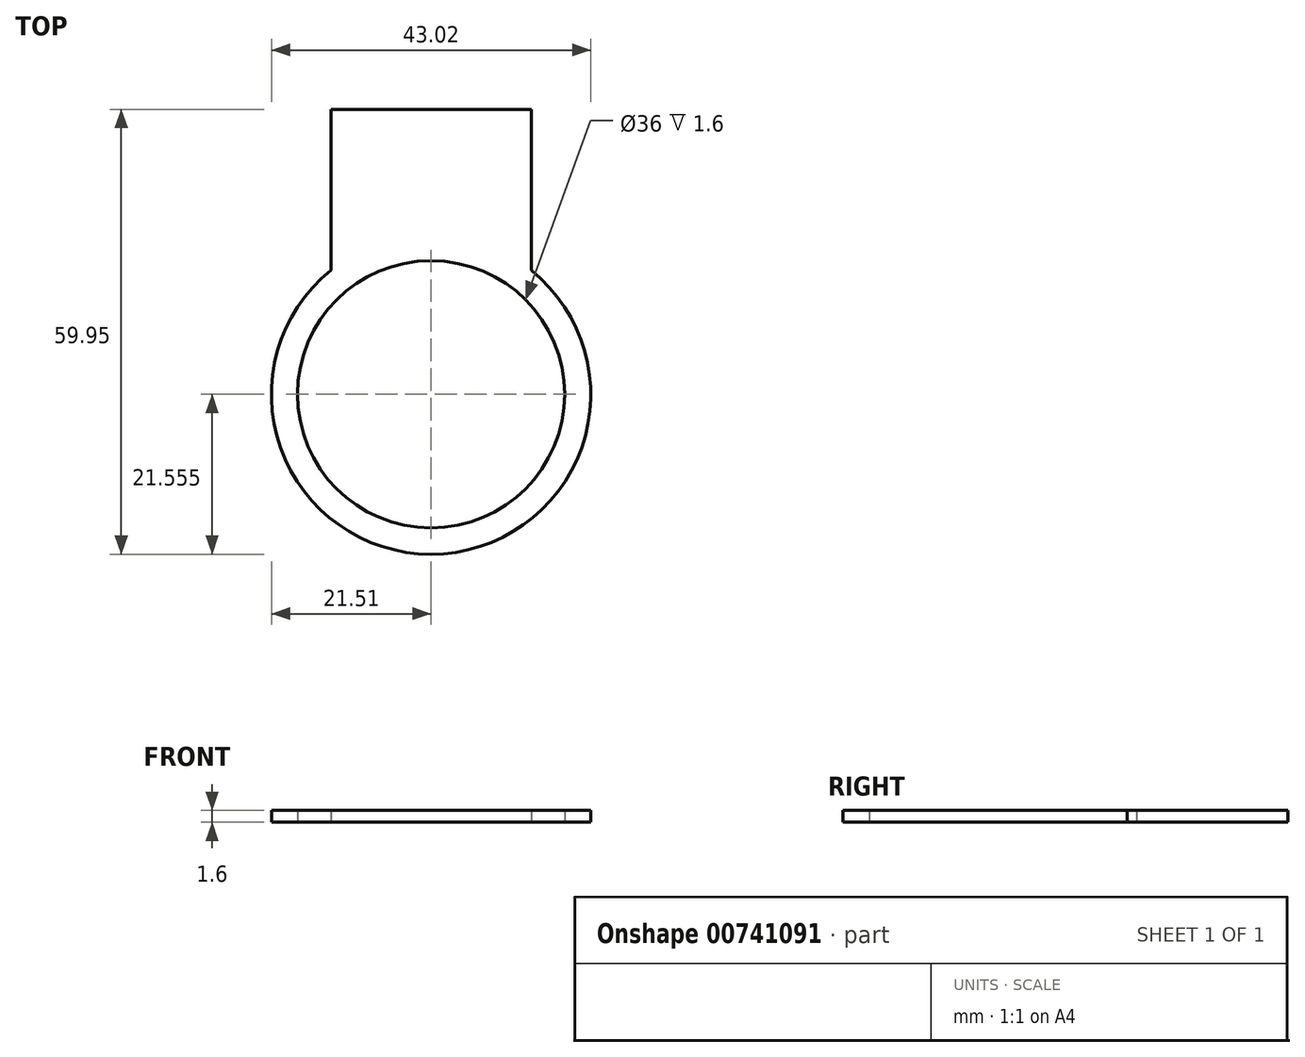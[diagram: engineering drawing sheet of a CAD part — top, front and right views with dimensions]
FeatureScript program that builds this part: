
annotation { "Feature Type Name" : "Feature", "Feature Type Description" : "" }
export const myFeature = defineFeature(function(context is Context, id is Id, definition is map)
    precondition{}
    {
        {
            var Q0;
            Q0=qCreatedBy(makeId("Top.planeOp"),FACE);
            var sketch = newSketch(context, id + "F0", { "sketchPlane" : qUnion([Q0])});
            skArc(sketch, "E0", {"start": v(-13.5, 8.26) * mm, "mid": v(0, -29.99) * mm, "end": v(13.5, 8.26) * mm});
            skLineSegment(sketch, "E1", {"start": v(13.5, 8.26) * mm, "end": v(13.5, 29.96) * mm});
            skArc(sketch, "E2", {"start": v(13.53, 29.96) * mm, "mid": v(13.5, 29.99) * mm, "end": v(13.47, 29.96) * mm});
            skLineSegment(sketch, "E3", {"start": v(-13.5, 29.96) * mm, "end": v(13.5, 29.96) * mm});
            skArc(sketch, "E4", {"start": v(13.5, 29.94) * mm, "mid": v(13.53, 29.96) * mm, "end": v(13.5, 29.99) * mm});
            skArc(sketch, "E5", {"start": v(-13.5, 29.99) * mm, "mid": v(-13.53, 29.96) * mm, "end": v(-13.5, 29.94) * mm});
            skLineSegment(sketch, "E6", {"start": v(-13.5, 8.26) * mm, "end": v(-13.5, 29.96) * mm});
            skArc(sketch, "E7", {"start": v(-13.48, 29.96) * mm, "mid": v(-13.5, 29.99) * mm, "end": v(-13.53, 29.96) * mm});
            skLineSegment(sketch, "E8", {"start": v(6.4, 18.46) * mm, "end": v(6.4, 19.26) * mm});
            skArc(sketch, "E9", {"start": v(6.42, 19.26) * mm, "mid": v(6.4, 19.29) * mm, "end": v(6.37, 19.26) * mm});
            skArc(sketch, "E10", {"start": v(6.37, 18.46) * mm, "mid": v(6.4, 18.44) * mm, "end": v(6.42, 18.46) * mm});
            skLineSegment(sketch, "E11", {"start": v(6.8, 18.86) * mm, "end": v(6, 18.86) * mm});
            skArc(sketch, "E12", {"start": v(6, 18.89) * mm, "mid": v(5.98, 18.86) * mm, "end": v(6, 18.84) * mm});
            skArc(sketch, "E13", {"start": v(6.8, 18.84) * mm, "mid": v(6.82, 18.86) * mm, "end": v(6.8, 18.89) * mm});
            skLineSegment(sketch, "E14", {"start": v(-6.8, 17.56) * mm, "end": v(-6.8, 18.96) * mm});
            skArc(sketch, "E15", {"start": v(-6.78, 18.96) * mm, "mid": v(-6.8, 18.99) * mm, "end": v(-6.83, 18.96) * mm});
            skArc(sketch, "E16", {"start": v(-6.83, 17.56) * mm, "mid": v(-6.8, 17.54) * mm, "end": v(-6.78, 17.56) * mm});
            skLineSegment(sketch, "E17", {"start": v(-7.5, 18.26) * mm, "end": v(-6.1, 18.26) * mm});
            skArc(sketch, "E18", {"start": v(-6.1, 18.24) * mm, "mid": v(-6.08, 18.26) * mm, "end": v(-6.1, 18.29) * mm});
            skArc(sketch, "E19", {"start": v(-7.5, 18.29) * mm, "mid": v(-7.53, 18.26) * mm, "end": v(-7.5, 18.24) * mm});
            skLineSegment(sketch, "E20", {"start": v(0, 18.16) * mm, "end": v(0, 20.36) * mm});
            skArc(sketch, "E21", {"start": v(0.03, 20.36) * mm, "mid": v(0, 20.39) * mm, "end": v(-0.03, 20.36) * mm});
            skArc(sketch, "E22", {"start": v(-0.03, 18.16) * mm, "mid": v(0, 18.14) * mm, "end": v(0.03, 18.16) * mm});
            skLineSegment(sketch, "E23", {"start": v(-1.1, 19.26) * mm, "end": v(1.1, 19.26) * mm});
            skArc(sketch, "E24", {"start": v(1.1, 19.24) * mm, "mid": v(1.12, 19.26) * mm, "end": v(1.1, 19.29) * mm});
            skArc(sketch, "E25", {"start": v(-1.1, 19.29) * mm, "mid": v(-1.13, 19.26) * mm, "end": v(-1.1, 19.24) * mm});
            skArc(sketch, "E26", {"start": v(0, -26.44) * mm, "mid": v(18, -8.44) * mm, "end": v(0, 9.56) * mm});
            skArc(sketch, "E27", {"start": v(0, 9.56) * mm, "mid": v(-18, -8.44) * mm, "end": v(0, -26.44) * mm});
            skSolve(sketch);
        }
        {
            var Q0;
            Q0=makeQuery(id+"F0.imprint","IMPRINT",FACE,{"disambiguationData":[TD([[makeQuery(id+"F0.imprint","IMPRINT",EDGE,{"derivedFrom":sQuery(id+"F0.wireOp",EDGE,"E26")}),-1.0]])]});
            extrude(context, id + "F1", {"entities" : qUnion([Q0]), "endBound" : BoundingType.SYMMETRIC, "depth" : 1.6 * mm, "offsetDistance" : 25 * mm});
        }
        {
            var Q0;
            Q0=makeQuery(id+"F1.opExtrude","CAP_FACE",FACE,{"disambiguationData":[OSD([sQuery(id+"F0.wireOp",EDGE,"E1"),sQuery(id+"F0.wireOp",EDGE,"ceca2dc5-4b51-4d0a-9e0b-030013c7a3e1"),sQuery(id+"F0.wireOp",EDGE,"E0"),sQuery(id+"F0.wireOp",EDGE,"8e6bffbf-1e1e-4fdc-b5db-a0290b015a5f"),sQuery(id+"F0.wireOp",EDGE,"db5c325e-766a-4718-8a78-7daab6099a77"),sQuery(id+"F0.wireOp",EDGE,"E3"),sQuery(id+"F0.wireOp",EDGE,"E6"),sQuery(id+"F0.wireOp",EDGE,"444f205d-ef0d-461a-a2ca-11d23d385707"),sQuery(id+"F0.wireOp",EDGE,"E26"),sQuery(id+"F0.wireOp",EDGE,"E27")])],"isStart":true});
            var sketch = newSketch(context, id + "F2", { "sketchPlane" : qUnion([Q0])});
            skLineSegment(sketch, "E28.0", {"start": v(-1.1, -19.26) * mm, "end": v(1.1, -19.26) * mm, "construction": true});
            skLineSegment(sketch, "E28.1", {"start": v(0, -18.16) * mm, "end": v(0, -20.36) * mm, "construction": true});
            skSolve(sketch);
        }
        {
            var Q0;
            Q0=makeQuery(id+"F1.opExtrude","CAP_FACE",FACE,{"disambiguationData":[OSD([sQuery(id+"F0.wireOp",EDGE,"E1"),sQuery(id+"F0.wireOp",EDGE,"ceca2dc5-4b51-4d0a-9e0b-030013c7a3e1"),sQuery(id+"F0.wireOp",EDGE,"E0"),sQuery(id+"F0.wireOp",EDGE,"8e6bffbf-1e1e-4fdc-b5db-a0290b015a5f"),sQuery(id+"F0.wireOp",EDGE,"db5c325e-766a-4718-8a78-7daab6099a77"),sQuery(id+"F0.wireOp",EDGE,"E3"),sQuery(id+"F0.wireOp",EDGE,"E6"),sQuery(id+"F0.wireOp",EDGE,"444f205d-ef0d-461a-a2ca-11d23d385707"),sQuery(id+"F0.wireOp",EDGE,"E26"),sQuery(id+"F0.wireOp",EDGE,"E27")])],"isStart":false});
            var sketch = newSketch(context, id + "F3", { "sketchPlane" : qUnion([Q0])});
            skLineSegment(sketch, "E29.0", {"start": v(-6.8, 17.56) * mm, "end": v(-6.8, 18.96) * mm, "construction": true});
            skLineSegment(sketch, "E30.0", {"start": v(-7.5, 18.26) * mm, "end": v(-6.1, 18.26) * mm, "construction": true});
            skLineSegment(sketch, "E31.0", {"start": v(6.8, 18.86) * mm, "end": v(6, 18.86) * mm, "construction": true});
            skLineSegment(sketch, "E32.0", {"start": v(6.4, 18.46) * mm, "end": v(6.4, 19.26) * mm, "construction": true});
            skSolve(sketch);
        }
    });
